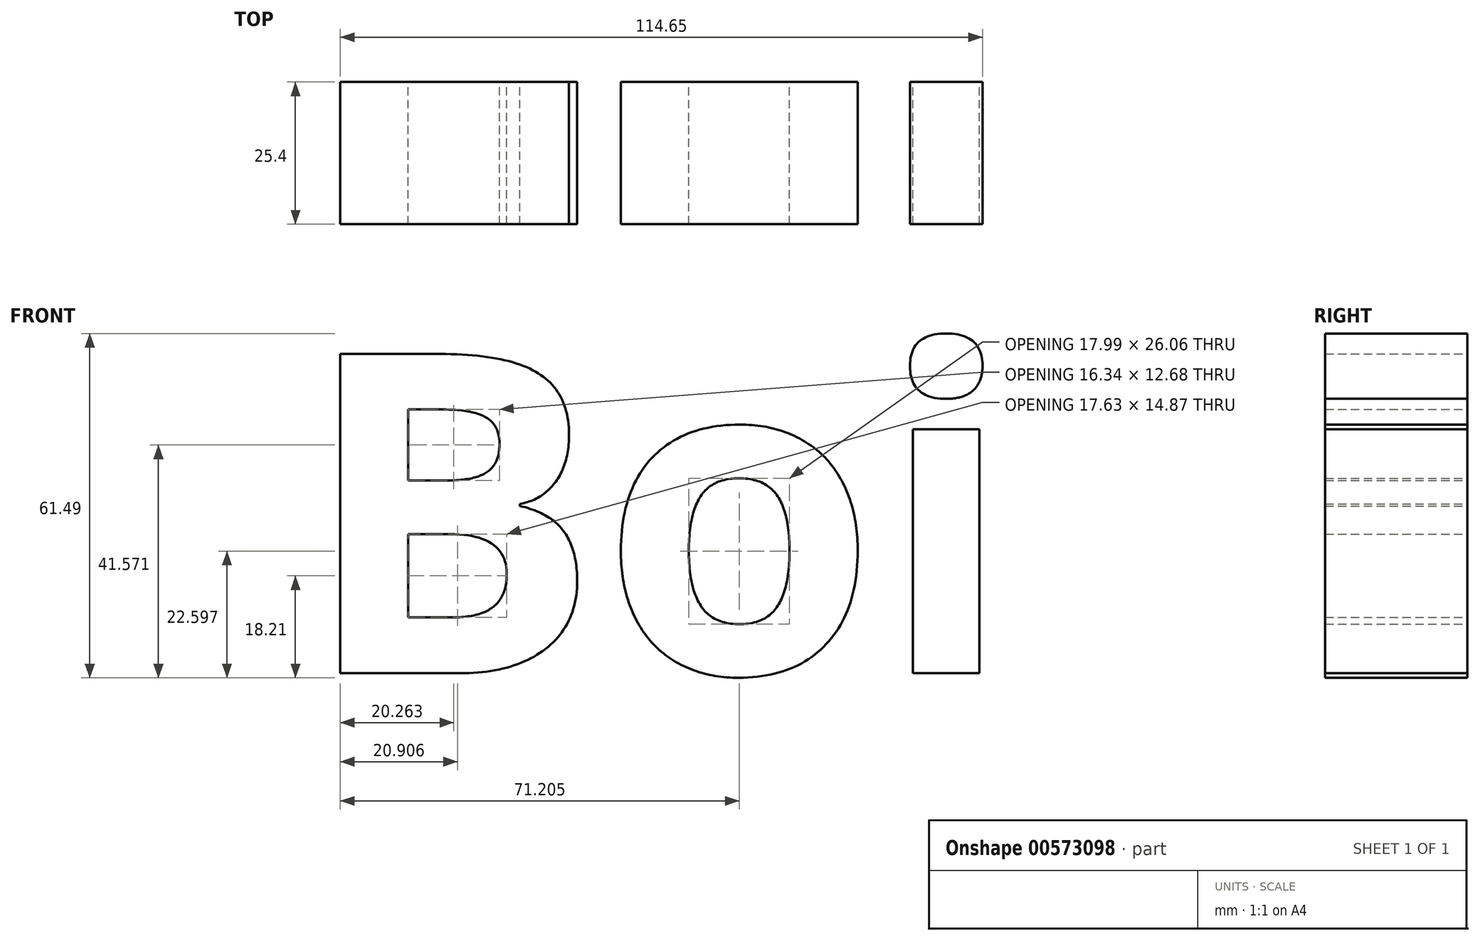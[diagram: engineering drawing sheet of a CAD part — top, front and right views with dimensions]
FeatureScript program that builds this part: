
annotation { "Feature Type Name" : "Feature", "Feature Type Description" : "" }
export const myFeature = defineFeature(function(context is Context, id is Id, definition is map)
    precondition{}
    {
        {
            var Q0;
            Q0=qCreatedBy(makeId("Front.planeOp"),FACE);
            var sketch = newSketch(context, id + "F0", { "sketchPlane" : qUnion([Q0])});
            skText(sketch, "E0", { "text": "Boi", "fontName": "OpenSans-Bold.ttf"});
            const initialGuessF0  = {"E0": [-0.07088, -0.01572, 1, 0, 0.05752]};
            skSetInitialGuess(sketch, initialGuessF0);
            skSolve(sketch);
        }
        {
            var Q0;
            Q0=makeQuery(id+"F0.imprint","IMPRINT",FACE,{"disambiguationData":[TD([[makeQuery(id+"F0.imprint","IMPRINT",EDGE,{"derivedFrom":sQuery(id+"F0.wireOp",EDGE,"E0.sketch_text.stroke-0")}),-1.0]])]});
            var Q1;
            Q1=makeQuery(id+"F0.imprint","IMPRINT",FACE,{"disambiguationData":[TD([[makeQuery(id+"F0.imprint","IMPRINT",EDGE,{"derivedFrom":sQuery(id+"F0.wireOp",EDGE,"E0.sketch_text.stroke-25")}),-1.0]])]});
            var Q2;
            Q2 = qSketchRegion(id + "F0", true);
            extrude(context, id + "F1", {"entities" : qUnion([Q0, Q1, Q2]), "depth" : 25.4 * mm, "offsetDistance" : 25.4 * mm});
        }
    });
